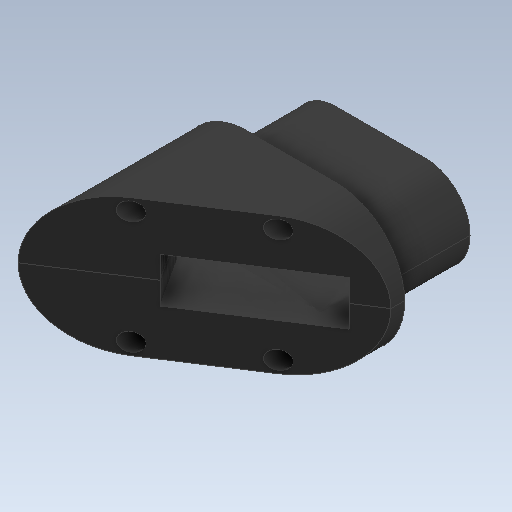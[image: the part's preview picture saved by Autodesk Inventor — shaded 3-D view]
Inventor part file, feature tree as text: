
AUTODESK INVENTOR PART (.ipt)
format: ipt  version: 2020 (Build 240168000, 168)  size: 302,080 bytes
history: native  units: mm
features: reference x9, sketch x6, extrude x6, other x5, projected_geometry x3, split x1, fillet x1, plane x1, hole x1
ambient origin geometry x8: Origin, YZ Plane, XZ Plane, XY Plane, X Axis, Y Axis, Z Axis, Center Point
bodies: Solid1 (feature_tree), Solid2 (feature_tree), Solid3 (feature_tree)
feature tree (33):
  sketch  "Sketch1"  dims[d0=30.0mm d1=0.0mm d2=70.0mm d3=0.0mm]
  extrude  "Extrusion1"  Depth=30.0mm TaperAngle=0.0deg
  extrude  "Extrusion2"  Depth=46.0mm
  extrude  "Extrusion3"  Depth=35.0mm TaperAngle=0.0deg
  extrude  "Extrusion4"  Depth=0.5mm
  extrude  "Extrusion5"  Depth=0.5mm
  extrude  "Extrusion6"  Depth=8.0mm
  split  "Split1"
  fillet  "Fillet1"  Radius=0.5mm
  plane  "Work Plane1"
  hole  "Hole1"  [1 undecoded]
  reference  "Reference1"
  sketch  "Sketch2"  dims[d4=100.0mm d5=0.0mm d6=46.0mm]
  reference  "Reference2"
  sketch  "Sketch3"  dims[d7=15.0mm d8=35.0mm d9=0.0mm]
  reference  "Reference3"
  reference  "Reference4"
  sketch  "Sketch5"  dims[d10=0.1mm d11=0.5mm]
  reference  "Reference10"
  reference  "Reference11"
  reference  "Reference12"
  reference  "Reference13"
  reference  "Reference14"
  sketch  "Sketch6"  dims[d12=0.5mm d13=0.5mm]
  projected_geometry  "Projected Loop1"
  sketch  "Sketch7"  dims[d14=0.5mm d15=0.5mm d16=0.5mm d17=20.1mm d18=0.0mm d19=6.0mm d20=40.0mm d21=0.0mm d22=8.0mm d23=-85.0mm d24=3.0mm d25=6.0mm d26=6.0mm d27=50.0mm d28=90.0deg d29=8.0mm d30=20.594885mm]
  projected_geometry  "Projected Loop2"
  projected_geometry  "Projected Loop3"
  other  "<userpath>\Documents\GitHub\OpenRaman\Hardware\OpenRaman.V1.iam"
  other  "OpenRaman.V1.iam"
  other  "SpectometerTube:1"
  other  "TCD1304AP:1"
  other  "PrismsGeometry:1"
note: 1 required parameter value undecoded (feature->parameter linkage not recoverable at this tier; creation-order binding heuristic only, values carry confidence <= 0.55)
